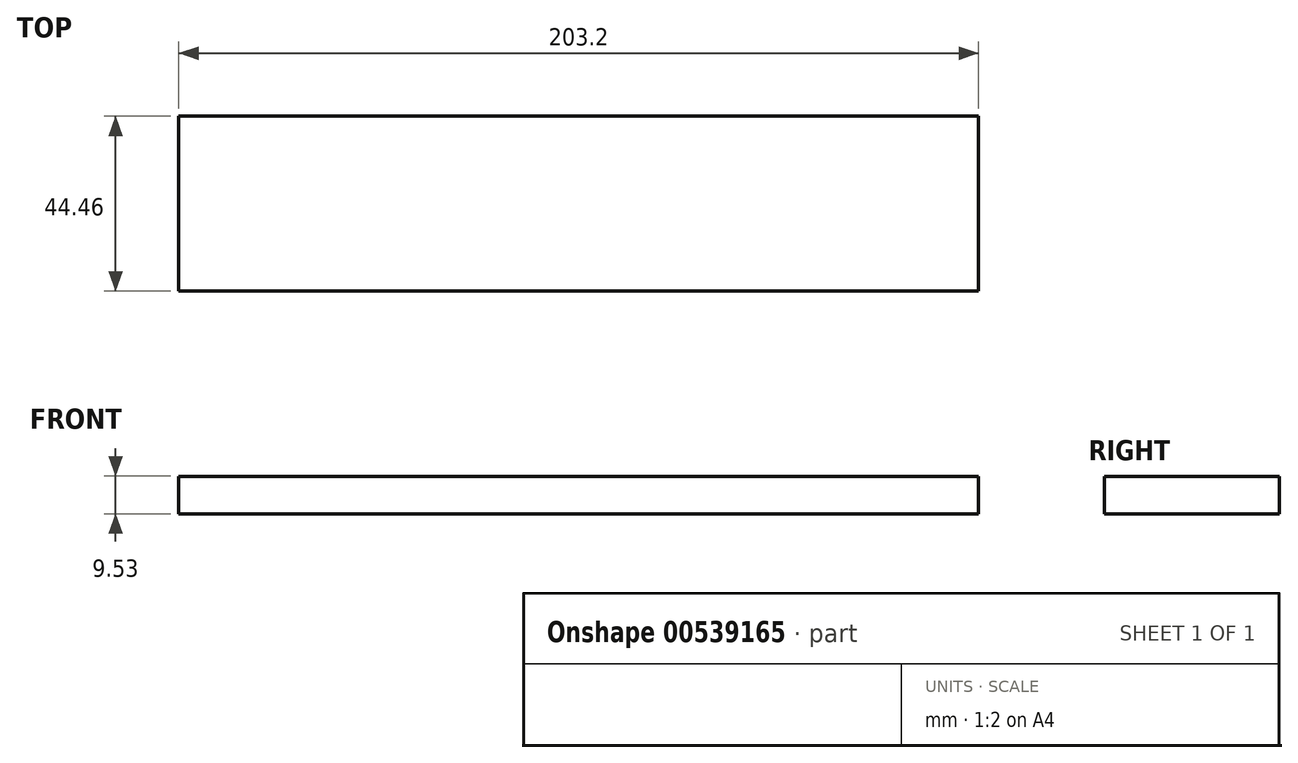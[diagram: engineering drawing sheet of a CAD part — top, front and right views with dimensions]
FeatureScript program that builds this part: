
annotation { "Feature Type Name" : "Feature", "Feature Type Description" : "" }
export const myFeature = defineFeature(function(context is Context, id is Id, definition is map)
    precondition{}
    {
        {
            var Q0;
            Q0=qCreatedBy(makeId("Top.planeOp"),FACE);
            var sketch = newSketch(context, id + "F0", { "sketchPlane" : qUnion([Q0])});
            skLineSegment(sketch, "E0.bottom", {"start": v(-101.6, 22.22) * mm, "end": v(101.6, 22.22) * mm});
            skLineSegment(sketch, "E0.top", {"start": v(-101.6, -22.22) * mm, "end": v(101.6, -22.22) * mm});
            skLineSegment(sketch, "E0.left", {"start": v(-101.6, 22.23) * mm, "end": v(-101.6, -22.22) * mm});
            skLineSegment(sketch, "E0.right", {"start": v(101.6, 22.22) * mm, "end": v(101.6, -22.22) * mm});
            skPoint(sketch, "E0.middle", {"position": v(0, 0) * mm});
            skSolve(sketch);
        }
        {
            var Q0;
            Q0=makeQuery(id+"F0.imprint","IMPRINT",FACE,{"disambiguationData":[TD([[makeQuery(id+"F0.imprint","IMPRINT",EDGE,{"derivedFrom":sQuery(id+"F0.wireOp",EDGE,"E0.bottom")}),-1.0]])]});
            extrude(context, id + "F1", {"entities" : qUnion([Q0]), "depth" : 9.52 * mm, "offsetDistance" : 25.4 * mm});
        }
    });
